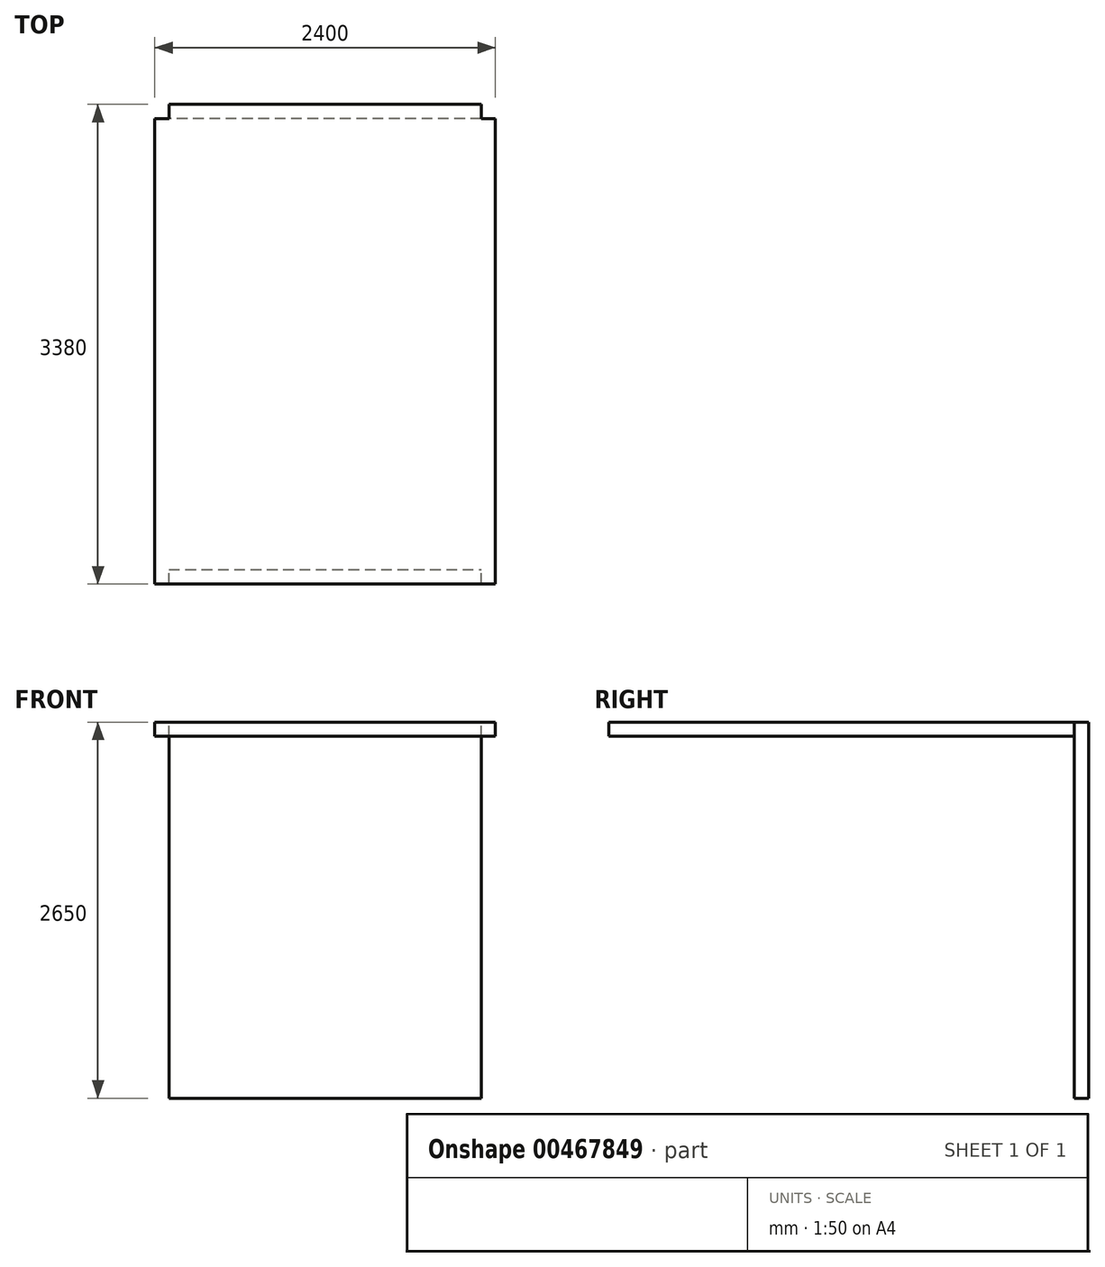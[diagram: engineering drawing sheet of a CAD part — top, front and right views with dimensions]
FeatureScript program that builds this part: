
annotation { "Feature Type Name" : "Feature", "Feature Type Description" : "" }
export const myFeature = defineFeature(function(context is Context, id is Id, definition is map)
    precondition{}
    {
        {
            var Q0;
            Q0=qCreatedBy(makeId("Top.planeOp"),FACE);
            var sketch = newSketch(context, id + "F0", { "sketchPlane" : qUnion([Q0])});
            skLineSegment(sketch, "E0.bottom", {"start": v(1200, -1690) * mm, "end": v(-1200, -1690) * mm});
            skLineSegment(sketch, "E0.top", {"start": v(1200, 1690) * mm, "end": v(-1200, 1690) * mm});
            skLineSegment(sketch, "E0.left", {"start": v(1200, -1690) * mm, "end": v(1200, 1690) * mm});
            skLineSegment(sketch, "E0.right", {"start": v(-1200, -1690) * mm, "end": v(-1200, 1690) * mm});
            skPoint(sketch, "E0.middle", {"position": v(0, 0) * mm});
            skLineSegment(sketch, "E1.bottom", {"start": v(-1200, 1690) * mm, "end": v(-1100, 1690) * mm});
            skLineSegment(sketch, "E1.top", {"start": v(-1200, -1690) * mm, "end": v(-1100, -1690) * mm});
            skLineSegment(sketch, "E1.left", {"start": v(-1200, 1690) * mm, "end": v(-1200, -1690) * mm});
            skLineSegment(sketch, "E1.right", {"start": v(-1100, 1690) * mm, "end": v(-1100, -1690) * mm});
            skLineSegment(sketch, "E2.bottom", {"start": v(1200, -1690) * mm, "end": v(1100, -1690) * mm});
            skLineSegment(sketch, "E2.top", {"start": v(1200, 1690) * mm, "end": v(1100, 1690) * mm});
            skLineSegment(sketch, "E2.right", {"start": v(1100, -1690) * mm, "end": v(1100, 1690) * mm});
            skLineSegment(sketch, "E3.top", {"start": v(1200, 1590) * mm, "end": v(-1200, 1590) * mm});
            skLineSegment(sketch, "E3.left", {"start": v(1200, 1690) * mm, "end": v(1200, 1590) * mm});
            skLineSegment(sketch, "E3.right", {"start": v(-1200, 1690) * mm, "end": v(-1200, 1590) * mm});
            skSolve(sketch);
        }
        {
            var Q0;
            {var subQ0=sQuery(id+"F0.wireOp",EDGE,"E0.bottom");Q0=makeQuery(id+"F0.imprint","IMPRINT",FACE,{"disambiguationData":[TD([[makeQuery(id+"F0.imprint","IMPRINT",EDGE,{"derivedFrom":subQ0}),-1.0]])]});}
            extrude(context, id + "F1", {"entities" : qUnion([Q0]), "depth" : -100 * mm});
        }
        {
            var Q0;
            {var subQ0=sQuery(id+"F0.wireOp",EDGE,"E1.top");Q0=makeQuery(id+"F0.imprint","IMPRINT",FACE,{"disambiguationData":[TD([[makeQuery(id+"F0.imprint","IMPRINT",EDGE,{"derivedFrom":subQ0}),1.0]])]});}
            var Q1;
            {var subQ0=sQuery(id+"F0.wireOp",EDGE,"E0.top");var subQ1=sQuery(id+"F0.wireOp",EDGE,"E1.right");var subQ2=makeQuery(id+"F0.imprint","INTERSECT",VERTEX,{"derivedFrom":[subQ1,subQ0]});Q1=makeQuery(id+"F0.imprint","IMPRINT",FACE,{"disambiguationData":[TD([[makeQuery(id+"F0.imprint","IMPRINT",EDGE,{"disambiguationData":[TD([[subQ2,-1.0]])],"derivedFrom":subQ1}),1.0]])]});}
            var Q2;
            {var subQ0=sQuery(id+"F0.wireOp",EDGE,"E2.bottom");Q2=makeQuery(id+"F0.imprint","IMPRINT",FACE,{"disambiguationData":[TD([[makeQuery(id+"F0.imprint","IMPRINT",EDGE,{"derivedFrom":subQ0}),-1.0]])]});}
            var Q3;
            {var subQ5=sQuery(id+"F0.wireOp",EDGE,"E3.left");Q3=makeQuery(id+"F0.imprint","IMPRINT",FACE,{"disambiguationData":[TD([[makeQuery(id+"F0.imprint","IMPRINT",EDGE,{"derivedFrom":subQ5}),-1.0]])]});}
            var Q4;
            {var subQ5=sQuery(id+"F0.wireOp",EDGE,"E3.right");Q4=makeQuery(id+"F0.imprint","IMPRINT",FACE,{"disambiguationData":[TD([[makeQuery(id+"F0.imprint","IMPRINT",EDGE,{"derivedFrom":subQ5}),1.0]])]});}
            extrude(context, id + "F2", {"entities" : qUnion([Q0, Q1, Q2, Q3, Q4]), "operationType" : NewBodyOperationType.ADD, "depth" : -2650 * mm});
        }
        {
            var Q0;
            Q0=makeQuery(id+"F1.opExtrude","CAP_FACE",FACE,{"disambiguationData":[OSD([sQuery(id+"F0.wireOp",EDGE,"E0.bottom"),sQuery(id+"F0.wireOp",EDGE,"E1.right"),sQuery(id+"F0.wireOp",EDGE,"E2.right"),sQuery(id+"F0.wireOp",EDGE,"E3.top")])],"isStart":false});
            var sketch = newSketch(context, id + "F3", { "sketchPlane" : qUnion([Q0])});
            skLineSegment(sketch, "E4.bottom", {"start": v(-1100, 1690) * mm, "end": v(1100, 1690) * mm});
            skLineSegment(sketch, "E4.top", {"start": v(-1100, 1590) * mm, "end": v(1100, 1590) * mm});
            skLineSegment(sketch, "E4.left", {"start": v(-1100, 1690) * mm, "end": v(-1100, 1590) * mm});
            skLineSegment(sketch, "E4.right", {"start": v(1100, 1690) * mm, "end": v(1100, 1590) * mm});
            skSolve(sketch);
        }
        {
            var Q0;
            Q0=makeQuery(id+"F3.imprint","IMPRINT",FACE,{"disambiguationData":[TD([[makeQuery(id+"F3.imprint","IMPRINT",EDGE,{"derivedFrom":sQuery(id+"F3.wireOp",EDGE,"E4.bottom")}),1.0]])]});
            extrude(context, id + "F4", {"entities" : qUnion([Q0]), "operationType" : NewBodyOperationType.ADD, "depth" : 0.1 * mm});
        }
    });
